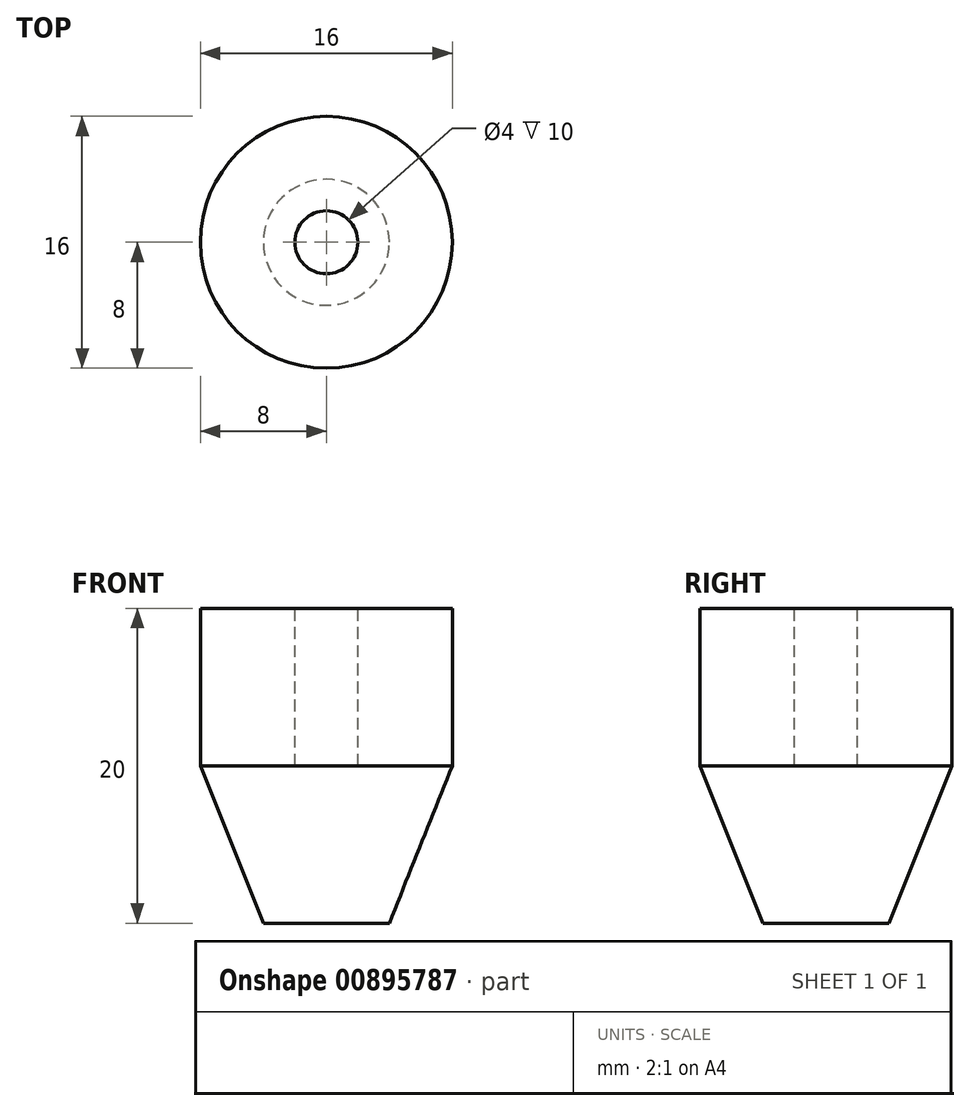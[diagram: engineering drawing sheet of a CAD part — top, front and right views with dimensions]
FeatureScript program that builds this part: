
annotation { "Feature Type Name" : "Feature", "Feature Type Description" : "" }
export const myFeature = defineFeature(function(context is Context, id is Id, definition is map)
    precondition{}
    {
        {
            var Q0;
            Q0=qCreatedBy(makeId("Front.planeOp"),FACE);
            var sketch = newSketch(context, id + "F0", { "sketchPlane" : qUnion([Q0])});
            skLineSegment(sketch, "E0.bottom", {"start": v(-4, 10) * mm, "end": v(4, 10) * mm});
            skLineSegment(sketch, "E0.top", {"start": v(0, -10) * mm, "end": v(4, -10) * mm});
            skLineSegment(sketch, "E0.left", {"start": v(-4, 10) * mm, "end": v(-4, 0) * mm});
            skLineSegment(sketch, "E0.right", {"start": v(4, 10) * mm, "end": v(4, -10) * mm});
            skPoint(sketch, "E0.middle", {"position": v(0, 0) * mm});
            skLineSegment(sketch, "E1", {"start": v(-4, 0) * mm, "end": v(0, -10) * mm});
            skPoint(sketch, "E2.orphan", {"position": v(-4, -10) * mm});
            skSolve(sketch);
        }
        {
            var Q0;
            Q0 = qSketchRegion(id + "F0", true);
            var Q1;
            Q1=sQuery(id+"F0.wireOp",EDGE,"E0.right");
            revolve(context, id + "F1", {"surfaceOperationType" : NewSurfaceOperationType.NEW, "entities" : qUnion([Q0]), "axis" : qUnion([Q1]), "revolveType" : RevolveType.FULL});
        }
        {
            var Q0;
            Q0=makeQuery(id+"F1.opRevolve","SWEPT_FACE",FACE,{"disambiguationData":[OSD([sQuery(id+"F0.wireOp",EDGE,"E0.bottom")])]});
            var sketch = newSketch(context, id + "F2", { "sketchPlane" : qUnion([Q0])});
            skCircle(sketch, "E3", {"center": v(4, 0) * mm, "radius": 2 * mm});
            skSolve(sketch);
        }
        {
            var Q0;
            Q0 = qSketchRegion(id + "F2", true);
            extrude(context, id + "F3", {"entities" : qUnion([Q0]), "operationType" : NewBodyOperationType.REMOVE, "oppositeDirection" : true, "depth" : 10 * mm, "offsetDistance" : 25 * mm});
        }
    });
